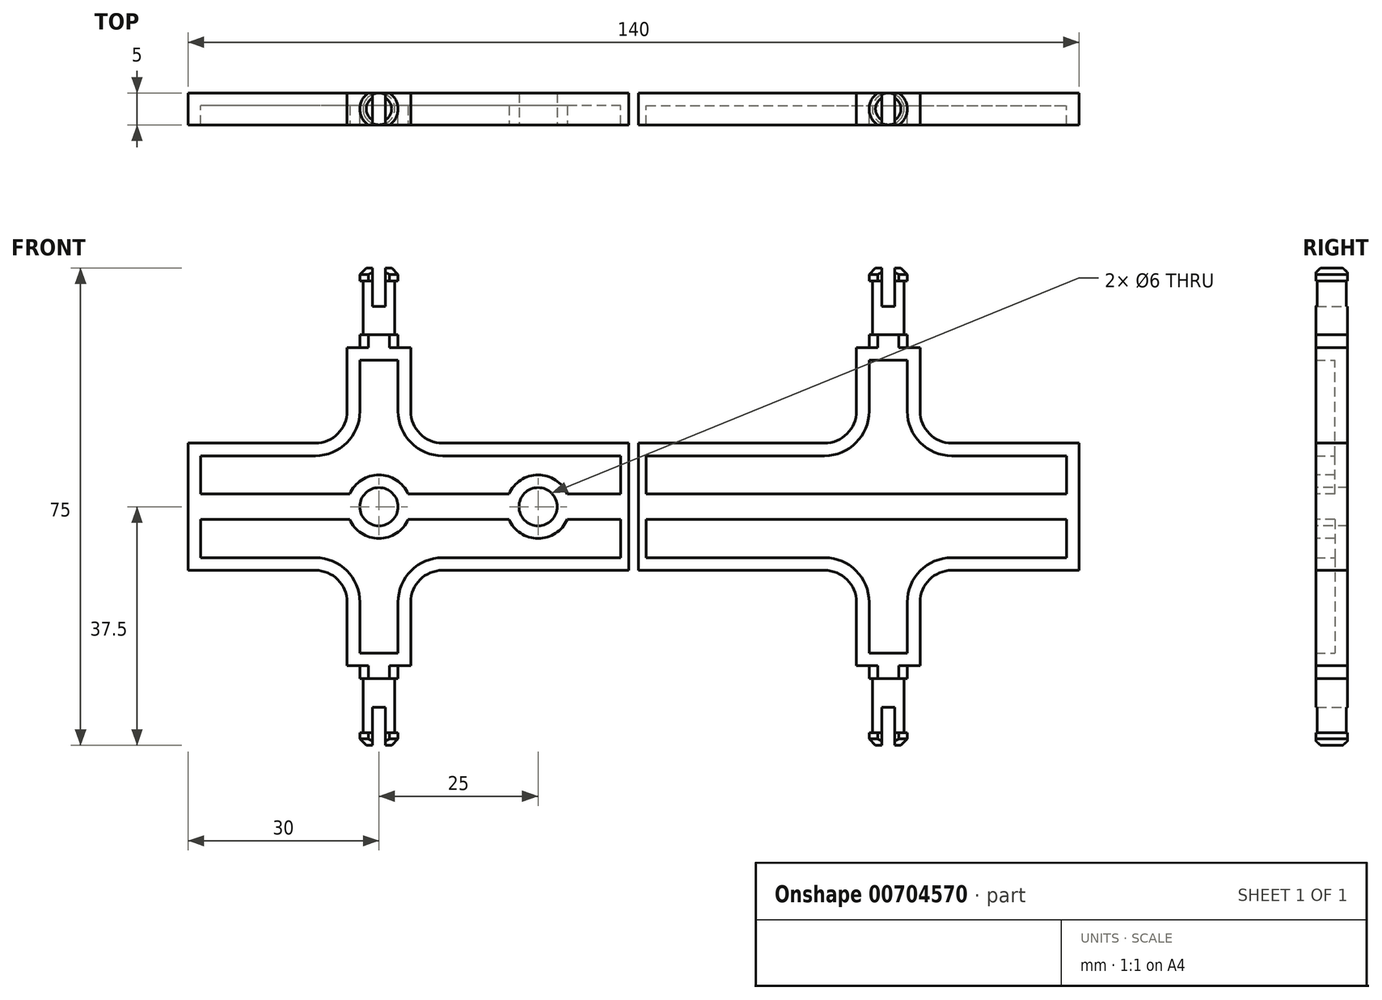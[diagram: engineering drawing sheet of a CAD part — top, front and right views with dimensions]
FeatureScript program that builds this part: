
annotation { "Feature Type Name" : "Feature", "Feature Type Description" : "" }
export const myFeature = defineFeature(function(context is Context, id is Id, definition is map)
    precondition{}
    {
        {
            var Q0;
            Q0=qCreatedBy(makeId("Front.planeOp"),FACE);
            var sketch = newSketch(context, id + "F0", { "sketchPlane" : qUnion([Q0])});
            skLineSegment(sketch, "E0.bottom", {"start": v(0, 0) * mm, "end": v(70, 0) * mm});
            skLineSegment(sketch, "E0.top", {"start": v(0, 10) * mm, "end": v(30, 10) * mm});
            skLineSegment(sketch, "E0.left", {"start": v(0, 0) * mm, "end": v(0, 10) * mm});
            skLineSegment(sketch, "E0.right", {"start": v(70, 0) * mm, "end": v(70, 10) * mm});
            skLineSegment(sketch, "E1.top", {"start": v(35, 25) * mm, "end": v(45, 25) * mm});
            skLineSegment(sketch, "E1.left", {"start": v(35, 15) * mm, "end": v(35, 25) * mm});
            skLineSegment(sketch, "E1.right", {"start": v(45, 15) * mm, "end": v(45, 25) * mm});
            skLineSegment(sketch, "E2.trimOffspring", {"start": v(50, 10) * mm, "end": v(70, 10) * mm});
            skPoint(sketch, "E3.visualSharp", {"position": v(35, 10) * mm});
            skArc(sketch, "E3.filletArc", {"start": v(30, 10) * mm, "mid": v(33.54, 11.46) * mm, "end": v(35, 15) * mm});
            skPoint(sketch, "E4.visualSharp", {"position": v(45, 10) * mm});
            skArc(sketch, "E4.filletArc", {"start": v(45, 15) * mm, "mid": v(46.46, 11.46) * mm, "end": v(50, 10) * mm});
            skSolve(sketch);
        }
        {
            var Q0;
            Q0 = qSketchRegion(id + "F0", true);
            extrude(context, id + "F1", {"entities" : qUnion([Q0]), "endBound" : BoundingType.SYMMETRIC, "depth" : 5 * mm, "offsetDistance" : 25 * mm});
        }
        {
            var Q0;
            Q0=makeQuery(id+"F1.opExtrude","CAP_FACE",FACE,{"disambiguationData":[OSD([sQuery(id+"F0.wireOp",EDGE,"E0.bottom"),sQuery(id+"F0.wireOp",EDGE,"E0.top"),sQuery(id+"F0.wireOp",EDGE,"E0.left"),sQuery(id+"F0.wireOp",EDGE,"E0.right"),sQuery(id+"F0.wireOp",EDGE,"E1.top"),sQuery(id+"F0.wireOp",EDGE,"E1.left"),sQuery(id+"F0.wireOp",EDGE,"E1.right"),sQuery(id+"F0.wireOp",EDGE,"E2.trimOffspring"),sQuery(id+"F0.wireOp",EDGE,"E3.filletArc"),sQuery(id+"F0.wireOp",EDGE,"E4.filletArc")])],"isStart":false});
            shell(context, id + "F2", {"entities" : qUnion([Q0]), "thickness" : 2 * mm});
        }
        {
            var Q0;
            Q0=qCreatedBy(makeId("Front.planeOp"),FACE);
            var sketch = newSketch(context, id + "F3", { "sketchPlane" : qUnion([Q0])});
            skLineSegment(sketch, "E5", {"start": v(37, 25) * mm, "end": v(40, 25) * mm});
            skLineSegment(sketch, "E6", {"start": v(40, 25) * mm, "end": v(40, 37.5) * mm});
            skLineSegment(sketch, "E7", {"start": v(40, 37.5) * mm, "end": v(37, 37.5) * mm});
            skLineSegment(sketch, "E8", {"start": v(37, 37.5) * mm, "end": v(37, 35.5) * mm});
            skLineSegment(sketch, "E9", {"start": v(37, 35.5) * mm, "end": v(37.5, 35.5) * mm});
            skLineSegment(sketch, "E10", {"start": v(37.5, 35.5) * mm, "end": v(37.5, 27) * mm});
            skLineSegment(sketch, "E11", {"start": v(37.5, 27) * mm, "end": v(37, 27) * mm});
            skLineSegment(sketch, "E12", {"start": v(37, 27) * mm, "end": v(37, 25) * mm});
            skSolve(sketch);
        }
        {
            var Q0;
            Q0 = qSketchRegion(id + "F3", true);
            var Q1;
            Q1=sQuery(id+"F3.wireOp",EDGE,"E6");
            revolve(context, id + "F4", {"operationType" : NewBodyOperationType.ADD, "surfaceOperationType" : NewSurfaceOperationType.NEW, "entities" : qUnion([Q0]), "axis" : qUnion([Q1]), "revolveType" : RevolveType.FULL});
        }
        {
            var Q0;
            Q0=makeQuery(id+"F4.opRevolve","SWEPT_EDGE",EDGE,{"disambiguationData":[OSD([sQuery(id+"F3.wireOp",EDGE,"E7"),sQuery(id+"F3.wireOp",EDGE,"E8")])]});
            chamfer(context, id + "F5", {"entities" : qUnion([Q0]), "width" : 1 * mm, "tangentPropagation" : true});
        }
        {
            var Q0;
            Q0=makeQuery(id+"F4.opRevolve","SWEPT_FACE",FACE,{"disambiguationData":[OSD([sQuery(id+"F3.wireOp",EDGE,"E7")])]});
            var sketch = newSketch(context, id + "F6", { "sketchPlane" : qUnion([Q0])});
            skLineSegment(sketch, "E13.bottom", {"start": v(79.2, -2.5) * mm, "end": v(0.8, -2.5) * mm});
            skLineSegment(sketch, "E13.top", {"start": v(79.2, 2.5) * mm, "end": v(0.8, 2.5) * mm});
            skLineSegment(sketch, "E13.left", {"start": v(79.2, -2.5) * mm, "end": v(79.2, 2.5) * mm});
            skLineSegment(sketch, "E13.right", {"start": v(0.8, -2.5) * mm, "end": v(0.8, 2.5) * mm});
            skPoint(sketch, "E13.middle", {"position": v(40, 0) * mm});
            skSolve(sketch);
        }
        {
            var Q0;
            Q0 = qSketchRegion(id + "F6", true);
            extrude(context, id + "F7", {"entities" : qUnion([Q0]), "operationType" : NewBodyOperationType.INTERSECT, "endBound" : BoundingType.THROUGH_ALL, "oppositeDirection" : true, "depth" : 25 * mm, "offsetDistance" : 25 * mm});
        }
        {
            var Q0;
            Q0=makeQuery(id+"F4.opRevolve","SWEPT_FACE",FACE,{"disambiguationData":[OSD([sQuery(id+"F3.wireOp",EDGE,"E7")])]});
            var sketch = newSketch(context, id + "F8", { "sketchPlane" : qUnion([Q0])});
            skLineSegment(sketch, "E14.bottom", {"start": v(41, -3.46) * mm, "end": v(39, -3.46) * mm});
            skLineSegment(sketch, "E14.top", {"start": v(41, 3.46) * mm, "end": v(39, 3.46) * mm});
            skLineSegment(sketch, "E14.left", {"start": v(41, -3.46) * mm, "end": v(41, 3.46) * mm});
            skLineSegment(sketch, "E14.right", {"start": v(39, -3.46) * mm, "end": v(39, 3.46) * mm});
            skPoint(sketch, "E14.middle", {"position": v(40, 0) * mm});
            skSolve(sketch);
        }
        {
            var Q0;
            Q0 = qSketchRegion(id + "F8", true);
            extrude(context, id + "F9", {"entities" : qUnion([Q0]), "operationType" : NewBodyOperationType.REMOVE, "oppositeDirection" : true, "depth" : 6 * mm, "offsetDistance" : 25 * mm});
        }
        {
            var Q0;
            Q0=makeQuery(id+"F1.opExtrude","SWEPT_BODY",BODY,{"disambiguationData":[OSD([sQuery(id+"F0.wireOp",EDGE,"E0.bottom"),sQuery(id+"F0.wireOp",EDGE,"E0.top"),sQuery(id+"F0.wireOp",EDGE,"E0.left"),sQuery(id+"F0.wireOp",EDGE,"E0.right"),sQuery(id+"F0.wireOp",EDGE,"E1.top"),sQuery(id+"F0.wireOp",EDGE,"E1.left"),sQuery(id+"F0.wireOp",EDGE,"E1.right"),sQuery(id+"F0.wireOp",EDGE,"E2.trimOffspring"),sQuery(id+"F0.wireOp",EDGE,"E3.filletArc"),sQuery(id+"F0.wireOp",EDGE,"E4.filletArc")])]});
            var Q1;
            Q1=qCreatedBy(makeId("Top.planeOp"),FACE);
            mirror(context, id + "F10", {"operationType" : NewBodyOperationType.ADD, "entities" : qUnion([Q0]), "mirrorPlane" : qUnion([Q1])});
        }
        {
            var Q0;
            Q0=makeQuery(id+"F1.opExtrude","SWEPT_BODY",BODY,{"disambiguationData":[OSD([sQuery(id+"F0.wireOp",EDGE,"E0.bottom"),sQuery(id+"F0.wireOp",EDGE,"E0.top"),sQuery(id+"F0.wireOp",EDGE,"E0.left"),sQuery(id+"F0.wireOp",EDGE,"E0.right"),sQuery(id+"F0.wireOp",EDGE,"E1.top"),sQuery(id+"F0.wireOp",EDGE,"E1.left"),sQuery(id+"F0.wireOp",EDGE,"E1.right"),sQuery(id+"F0.wireOp",EDGE,"E2.trimOffspring"),sQuery(id+"F0.wireOp",EDGE,"E3.filletArc"),sQuery(id+"F0.wireOp",EDGE,"E4.filletArc")])]});
            var Q1;
            Q1=qCreatedBy(makeId("Right.planeOp"),FACE);
            mirror(context, id + "F11", {"entities" : qUnion([Q0]), "mirrorPlane" : qUnion([Q1])});
        }
        {
            var Q0;
            {var subQ0=makeQuery(id+"F7.boolean.opBoolean","MERGE",FACE,{"derivedFrom":[makeQuery(id+"F1.opExtrude","CAP_FACE",FACE,{"disambiguationData":[OSD([sQuery(id+"F0.wireOp",EDGE,"E0.bottom"),sQuery(id+"F0.wireOp",EDGE,"E0.top"),sQuery(id+"F0.wireOp",EDGE,"E0.left"),sQuery(id+"F0.wireOp",EDGE,"E0.right"),sQuery(id+"F0.wireOp",EDGE,"E1.top"),sQuery(id+"F0.wireOp",EDGE,"E1.left"),sQuery(id+"F0.wireOp",EDGE,"E1.right"),sQuery(id+"F0.wireOp",EDGE,"E2.trimOffspring"),sQuery(id+"F0.wireOp",EDGE,"E3.filletArc"),sQuery(id+"F0.wireOp",EDGE,"E4.filletArc")])],"isStart":false}),makeQuery(id+"F7.boolean.toolComplement.opBoolean","COPY",FACE,{"derivedFrom":makeQuery(id+"F7.opExtrude","SWEPT_FACE",FACE,{"disambiguationData":[OSD([sQuery(id+"F6.wireOp",EDGE,"E13.bottom")])]})})]});Q0=makeQuery(id+"F11.opPattern","COPY",FACE,{"derivedFrom":makeQuery(id+"F10.boolean.opBoolean","MERGE",FACE,{"derivedFrom":[subQ0,makeQuery(id+"F10.opPattern","COPY",FACE,{"derivedFrom":subQ0,"instanceName":"1"})]}),"instanceName":"1"});}
            var sketch = newSketch(context, id + "F12", { "sketchPlane" : qUnion([Q0])});
            skCircle(sketch, "E15", {"center": v(-40, 0) * mm, "radius": 5 * mm});
            skCircle(sketch, "E16", {"center": v(-15, 0) * mm, "radius": 5 * mm});
            skSolve(sketch);
        }
        {
            var Q0;
            Q0 = qSketchRegion(id + "F12", true);
            extrude(context, id + "F13", {"entities" : qUnion([Q0]), "operationType" : NewBodyOperationType.ADD, "endBound" : BoundingType.UP_TO_NEXT, "oppositeDirection" : true, "depth" : 25 * mm, "offsetDistance" : 25 * mm});
        }
        {
            var Q0;
            {var subQ0=makeQuery(id+"F7.boolean.opBoolean","MERGE",FACE,{"derivedFrom":[makeQuery(id+"F1.opExtrude","CAP_FACE",FACE,{"disambiguationData":[OSD([sQuery(id+"F0.wireOp",EDGE,"E0.bottom"),sQuery(id+"F0.wireOp",EDGE,"E0.top"),sQuery(id+"F0.wireOp",EDGE,"E0.left"),sQuery(id+"F0.wireOp",EDGE,"E0.right"),sQuery(id+"F0.wireOp",EDGE,"E1.top"),sQuery(id+"F0.wireOp",EDGE,"E1.left"),sQuery(id+"F0.wireOp",EDGE,"E1.right"),sQuery(id+"F0.wireOp",EDGE,"E2.trimOffspring"),sQuery(id+"F0.wireOp",EDGE,"E3.filletArc"),sQuery(id+"F0.wireOp",EDGE,"E4.filletArc")])],"isStart":false}),makeQuery(id+"F7.boolean.toolComplement.opBoolean","COPY",FACE,{"derivedFrom":makeQuery(id+"F7.opExtrude","SWEPT_FACE",FACE,{"disambiguationData":[OSD([sQuery(id+"F6.wireOp",EDGE,"E13.bottom")])]})})]});Q0=makeQuery(id+"F13.boolean.opBoolean","MERGE",FACE,{"derivedFrom":[makeQuery(id+"F11.opPattern","COPY",FACE,{"derivedFrom":makeQuery(id+"F10.boolean.opBoolean","MERGE",FACE,{"derivedFrom":[subQ0,makeQuery(id+"F10.opPattern","COPY",FACE,{"derivedFrom":subQ0,"instanceName":"1"})]}),"instanceName":"1"}),makeQuery(id+"F13.opExtrude","CAP_FACE",FACE,{"disambiguationData":[OSD([sQuery(id+"F12.wireOp",EDGE,"E15")])],"isStart":true}),makeQuery(id+"F13.opExtrude","CAP_FACE",FACE,{"disambiguationData":[OSD([sQuery(id+"F12.wireOp",EDGE,"E16")])],"isStart":true})]});}
            var sketch = newSketch(context, id + "F14", { "sketchPlane" : qUnion([Q0])});
            skPoint(sketch, "E17", {"position": v(-40, 0) * mm});
            skPoint(sketch, "E18", {"position": v(-15, 0) * mm});
            skSolve(sketch);
        }
        {
            var Q0;
            Q0=sQuery(id+"F14.wireOp",VERTEX,"E17");
            var Q1;
            Q1=sQuery(id+"F14.wireOp",VERTEX,"E18");
            var Q2;
            Q2=makeQuery(id+"F11.opPattern","COPY",BODY,{"derivedFrom":makeQuery(id+"F1.opExtrude","SWEPT_BODY",BODY,{"disambiguationData":[OSD([sQuery(id+"F0.wireOp",EDGE,"E0.bottom"),sQuery(id+"F0.wireOp",EDGE,"E0.top"),sQuery(id+"F0.wireOp",EDGE,"E0.left"),sQuery(id+"F0.wireOp",EDGE,"E0.right"),sQuery(id+"F0.wireOp",EDGE,"E1.top"),sQuery(id+"F0.wireOp",EDGE,"E1.left"),sQuery(id+"F0.wireOp",EDGE,"E1.right"),sQuery(id+"F0.wireOp",EDGE,"E2.trimOffspring"),sQuery(id+"F0.wireOp",EDGE,"E3.filletArc"),sQuery(id+"F0.wireOp",EDGE,"E4.filletArc")])]}),"instanceName":"1"});
            hole(context, id + "F15", {"style" : HoleStyle.SIMPLE, "endStyle" : HoleEndStyle.THROUGH, "holeDiameter" : 6 * mm, "majorDiameter" : 5 * mm, "isTappedThrough" : true, "tappedDepth" : 12 * mm, "tapClearance" : 3, "locations" : qUnion([Q0, Q1]), "scope" : qUnion([Q2])});
        }
    });
